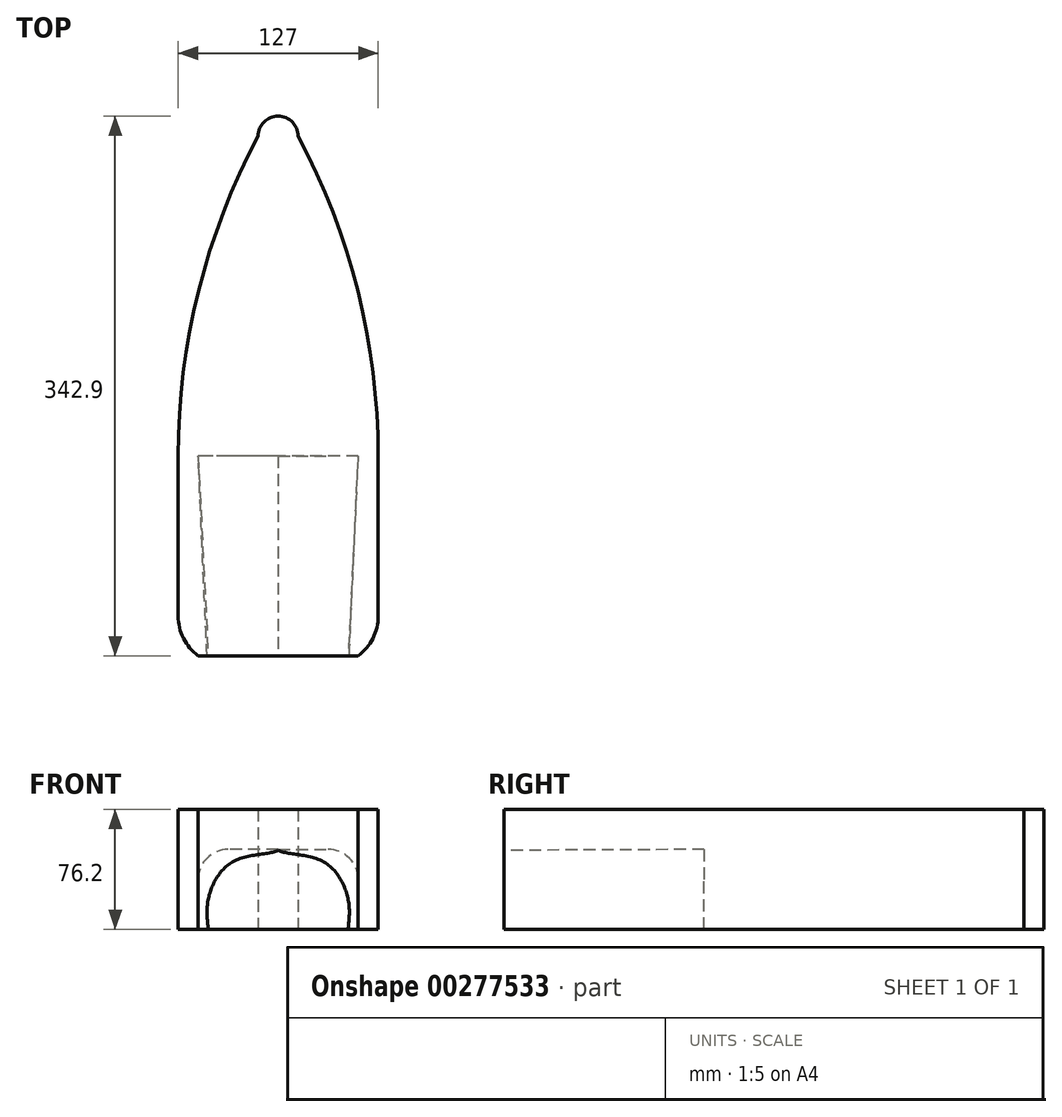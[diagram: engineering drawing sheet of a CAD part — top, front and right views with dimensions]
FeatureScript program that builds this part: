
annotation { "Feature Type Name" : "Feature", "Feature Type Description" : "" }
export const myFeature = defineFeature(function(context is Context, id is Id, definition is map)
    precondition{}
    {
        {
            var Q0;
            Q0=qCreatedBy(makeId("Top.planeOp"),FACE);
            var sketch = newSketch(context, id + "F0", { "sketchPlane" : qUnion([Q0])});
            skLineSegment(sketch, "E0", {"start": v(0, 0) * mm, "end": v(0, 203.2) * mm});
            skLineSegment(sketch, "E1", {"start": v(-63.5, 0) * mm, "end": v(63.5, 0) * mm});
            skLineSegment(sketch, "E2", {"start": v(0, 0) * mm, "end": v(0, -127) * mm});
            skLineSegment(sketch, "E3", {"start": v(0, 203.2) * mm, "end": v(-63.5, 203.2) * mm});
            skLineSegment(sketch, "E4", {"start": v(-63.5, 203.2) * mm, "end": v(-63.5, 0) * mm});
            skLineSegment(sketch, "E5", {"start": v(0, 203.2) * mm, "end": v(63.5, 203.2) * mm});
            skLineSegment(sketch, "E6", {"start": v(63.5, 203.2) * mm, "end": v(63.5, 0) * mm});
            skLineSegment(sketch, "E7", {"start": v(-63.5, 0) * mm, "end": v(-63.5, -127) * mm});
            skLineSegment(sketch, "E8", {"start": v(-63.5, -127) * mm, "end": v(0, -127) * mm});
            skLineSegment(sketch, "E9", {"start": v(63.5, -127) * mm, "end": v(63.5, 0) * mm});
            skLineSegment(sketch, "E10", {"start": v(63.5, -127) * mm, "end": v(0, -127) * mm});
            skLineSegment(sketch, "E11", {"start": v(0, -127) * mm, "end": v(-50.8, -127) * mm});
            skLineSegment(sketch, "E12", {"start": v(0, -127) * mm, "end": v(50.8, -127) * mm});
            skLineSegment(sketch, "E13", {"start": v(0, 203.2) * mm, "end": v(0, 215.9) * mm});
            skLineSegment(sketch, "E14", {"start": v(-63.5, -127) * mm, "end": v(-63.5, -101.6) * mm});
            skLineSegment(sketch, "E15", {"start": v(63.5, -127) * mm, "end": v(63.5, -101.6) * mm});
            skLineSegment(sketch, "E16", {"start": v(0, 203.2) * mm, "end": v(-12.7, 203.2) * mm});
            skLineSegment(sketch, "E17", {"start": v(0, 203.2) * mm, "end": v(12.7, 203.2) * mm});
            skArc(sketch, "E18", {"start": v(50.8, -127) * mm, "mid": v(60.15, -115.8) * mm, "end": v(63.5, -101.6) * mm});
            skArc(sketch, "E19", {"start": v(-63.5, -101.6) * mm, "mid": v(-60.15, -115.8) * mm, "end": v(-50.8, -127) * mm});
            skArc(sketch, "E20", {"start": v(12.7, 203.2) * mm, "mid": v(0, 215.9) * mm, "end": v(-12.7, 203.2) * mm});
            skArc(sketch, "E21", {"start": v(-12.7, 203.2) * mm, "mid": v(-50.6, 104.73) * mm, "end": v(-63.5, 0) * mm});
            skArc(sketch, "E22", {"start": v(63.5, 0) * mm, "mid": v(50.6, 104.73) * mm, "end": v(12.7, 203.2) * mm});
            skSolve(sketch);
        }
        {
            var Q0;
            {var subQ0=sQuery(id+"F0.wireOp",EDGE,"E0");Q0=makeQuery(id+"F0.imprint","IMPRINT",FACE,{"disambiguationData":[TD([[makeQuery(id+"F0.imprint","IMPRINT",EDGE,{"derivedFrom":subQ0}),-1.0]])]});}
            var Q1;
            {var subQ0=sQuery(id+"F0.wireOp",EDGE,"E0");Q1=makeQuery(id+"F0.imprint","IMPRINT",FACE,{"disambiguationData":[TD([[makeQuery(id+"F0.imprint","IMPRINT",EDGE,{"derivedFrom":subQ0}),1.0]])]});}
            var Q2;
            {var subQ0=sQuery(id+"F0.wireOp",EDGE,"E13");Q2=makeQuery(id+"F0.imprint","IMPRINT",FACE,{"disambiguationData":[TD([[makeQuery(id+"F0.imprint","IMPRINT",EDGE,{"derivedFrom":subQ0}),-1.0]])]});}
            var Q3;
            {var subQ0=sQuery(id+"F0.wireOp",EDGE,"E13");Q3=makeQuery(id+"F0.imprint","IMPRINT",FACE,{"disambiguationData":[TD([[makeQuery(id+"F0.imprint","IMPRINT",EDGE,{"derivedFrom":subQ0}),1.0]])]});}
            var Q4;
            {var subQ1=sQuery(id+"F0.wireOp",EDGE,"E2");Q4=makeQuery(id+"F0.imprint","IMPRINT",FACE,{"disambiguationData":[TD([[makeQuery(id+"F0.imprint","IMPRINT",EDGE,{"derivedFrom":subQ1}),-1.0]])]});}
            var Q5;
            {var subQ1=sQuery(id+"F0.wireOp",EDGE,"E2");Q5=makeQuery(id+"F0.imprint","IMPRINT",FACE,{"disambiguationData":[TD([[makeQuery(id+"F0.imprint","IMPRINT",EDGE,{"derivedFrom":subQ1}),1.0]])]});}
            extrude(context, id + "F1", {"entities" : qUnion([Q0, Q1, Q2, Q3, Q4, Q5]), "depth" : 76.2 * mm});
        }
        {
            var Q0;
            Q0=qCreatedBy(makeId("Front.planeOp"),FACE);
            cPlane(context, id + "F2", {"entities" : qUnion([Q0]), "cplaneType" : CPlaneType.OFFSET, "offset" : 127 * mm, "width" : 152.4 * mm, "height" : 152.4 * mm});
        }
        {
            var Q0;
            Q0=qCreatedBy(id+"F2.planeOp",FACE);
            cPlane(context, id + "F3", {"entities" : qUnion([Q0]), "cplaneType" : CPlaneType.OFFSET, "offset" : 127 * mm, "width" : 152.4 * mm, "height" : 152.4 * mm});
        }
        {
            var Q0;
            Q0=qCreatedBy(makeId("Front.planeOp"),FACE);
            var sketch = newSketch(context, id + "F4", { "sketchPlane" : qUnion([Q0])});
            skLineSegment(sketch, "E23.bottom", {"start": v(0, 0) * mm, "end": v(-50.8, 0) * mm});
            skLineSegment(sketch, "E23.top", {"start": v(0, 50.8) * mm, "end": v(-31.75, 50.8) * mm});
            skLineSegment(sketch, "E23.right", {"start": v(-50.8, 0) * mm, "end": v(-50.8, 31.75) * mm});
            skPoint(sketch, "E23.middle", {"position": v(0, 0) * mm});
            skArc(sketch, "E24", {"start": v(-31.75, 50.8) * mm, "mid": v(-45.22, 45.22) * mm, "end": v(-50.8, 31.75) * mm});
            skLineSegment(sketch, "E25", {"start": v(0, 0) * mm, "end": v(0, 50.8) * mm, "construction": true});
            skLineSegment(sketch, "E26.MirrorCS", {"start": v(0, 0) * mm, "end": v(50.8, 0) * mm});
            skLineSegment(sketch, "E27.MirrorCS", {"start": v(50.8, 0) * mm, "end": v(50.8, 31.75) * mm});
            skArc(sketch, "E28.MirrorCS", {"start": v(31.75, 50.8) * mm, "mid": v(45.22, 45.22) * mm, "end": v(50.8, 31.75) * mm});
            skLineSegment(sketch, "E29.MirrorCS", {"start": v(0, 50.8) * mm, "end": v(31.75, 50.8) * mm});
            skSolve(sketch);
        }
        {
            var Q0;
            Q0=qCreatedBy(id+"F2.planeOp",FACE);
            var sketch = newSketch(context, id + "F5", { "sketchPlane" : qUnion([Q0])});
            skLineSegment(sketch, "E30", {"start": v(0, 0) * mm, "end": v(44.45, 0) * mm});
            skFitSpline(sketch, "E31", {"points": [v(44.45, 0) * mm, v(44.65, 18.01) * mm, v(28.6, 43.08) * mm, v(0, 50.19) * mm], "startDerivative": vector(3.9, 55.53) * mm, "endDerivative": vector(-52.19, 24.2) * mm});
            skLineSegment(sketch, "E32", {"start": v(0, 0) * mm, "end": v(0, 50.19) * mm, "construction": true});
            skLineSegment(sketch, "E33.MirrorCS", {"start": v(0, 0) * mm, "end": v(-44.45, 0) * mm});
            skFitSpline(sketch, "E34.MirrorCS", {"points": [v(-44.45, 0) * mm, v(-44.65, 18.01) * mm, v(-28.6, 43.08) * mm, v(0, 50.19) * mm], "startDerivative": vector(-3.9, 55.53) * mm, "endDerivative": vector(52.19, 24.2) * mm});
            skSolve(sketch);
        }
        {
            var Q0;
            Q0=qCreatedBy(id+"F3.planeOp",FACE);
            var sketch = newSketch(context, id + "F6", { "sketchPlane" : qUnion([Q0])});
            skLineSegment(sketch, "E35", {"start": v(0, 0) * mm, "end": v(0, 8.01) * mm, "construction": true});
            skLineSegment(sketch, "E36", {"start": v(0, 0) * mm, "end": v(7.28, 0) * mm});
            skLineSegment(sketch, "E37", {"start": v(7.28, 0) * mm, "end": v(0, 8.01) * mm});
            skLineSegment(sketch, "E38.MirrorCS", {"start": v(0, 0) * mm, "end": v(-7.28, 0) * mm});
            skLineSegment(sketch, "E39.MirrorCS", {"start": v(-7.28, 0) * mm, "end": v(0, 8.01) * mm});
            skSolve(sketch);
        }
        {
            var Q0;
            Q0=makeQuery(id+"F4.imprint","IMPRINT",FACE,{"disambiguationData":[TD([[makeQuery(id+"F4.imprint","IMPRINT",EDGE,{"derivedFrom":sQuery(id+"F4.wireOp",EDGE,"E23.bottom")}),-1.0]])]});
            var Q1;
            Q1=makeQuery(id+"F5.imprint","IMPRINT",FACE,{"disambiguationData":[TD([[makeQuery(id+"F5.imprint","IMPRINT",EDGE,{"derivedFrom":sQuery(id+"F5.wireOp",EDGE,"E30")}),1.0]])]});
            var Q2;
            Q2=sQuery(id+"F4.wireOp",VERTEX,"E23.right.start");
            var Q3;
            Q3=sQuery(id+"F5.wireOp",VERTEX,"2b1e45c9-e8a8-4908-b833-9778dc6329120.MirrorCS.0.internal");
            var Q4;
            Q4=sQuery(id+"F6.wireOp",VERTEX,"E38.MirrorCS.end");
            loft(context, id + "F7", {"sheetProfilesArray" : [{ "sheetProfileEntities" : qUnion([Q0]) }, { "sheetProfileEntities" : qUnion([Q1]) }], "connections" : [{ "connectionEntities" : qUnion([Q2, Q3, Q4]), "connectionEdgeQueries" : qUnion([]), "connectionEdgeParameters" : [] }]});
        }
    });
